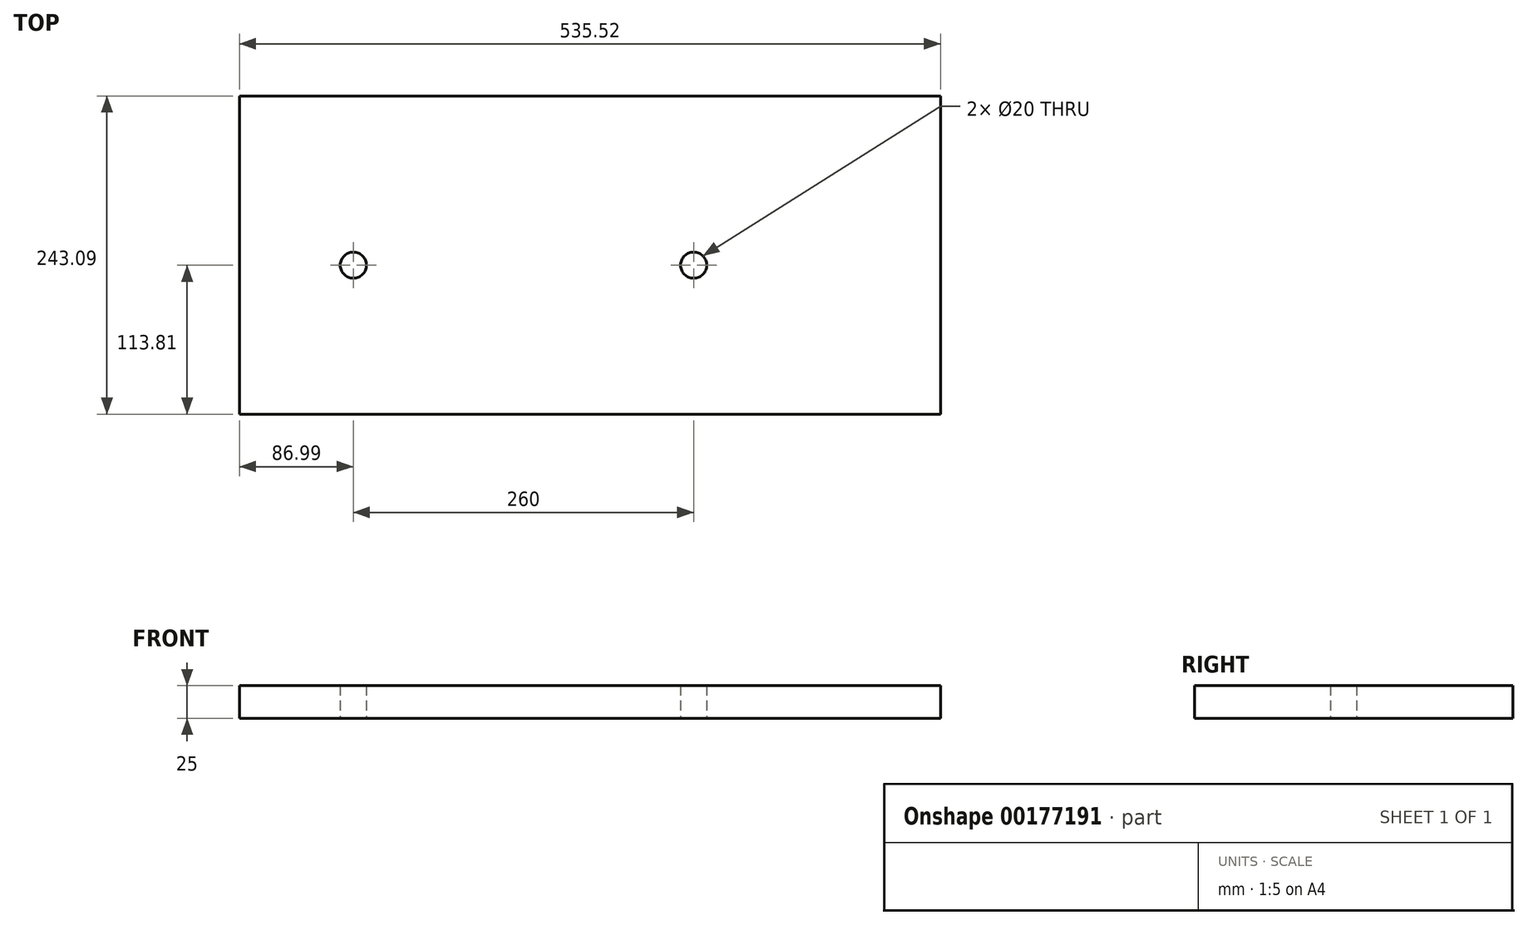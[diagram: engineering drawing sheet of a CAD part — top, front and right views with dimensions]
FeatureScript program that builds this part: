
annotation { "Feature Type Name" : "Feature", "Feature Type Description" : "" }
export const myFeature = defineFeature(function(context is Context, id is Id, definition is map)
    precondition{}
    {
        {
            var Q0;
            Q0=qCreatedBy(makeId("Top.planeOp"),FACE);
            var sketch = newSketch(context, id + "F0", { "sketchPlane" : qUnion([Q0])});
            skLineSegment(sketch, "E0.bottom", {"start": v(-206.99, 129.28) * mm, "end": v(328.53, 129.28) * mm});
            skLineSegment(sketch, "E0.top", {"start": v(-206.99, -113.8) * mm, "end": v(328.53, -113.8) * mm});
            skLineSegment(sketch, "E0.left", {"start": v(-206.99, 129.28) * mm, "end": v(-206.99, -113.8) * mm});
            skLineSegment(sketch, "E0.right", {"start": v(328.53, 129.28) * mm, "end": v(328.53, -113.8) * mm});
            skCircle(sketch, "E1", {"center": v(-120, 0) * mm, "radius": 10 * mm});
            skCircle(sketch, "E2", {"center": v(140, 0) * mm, "radius": 10 * mm});
            skSolve(sketch);
        }
        {
            var Q0;
            Q0 = qSketchRegion(id + "F0", true);
            extrude(context, id + "F1", {"entities" : qUnion([Q0]), "depth" : 25 * mm});
        }
    });
